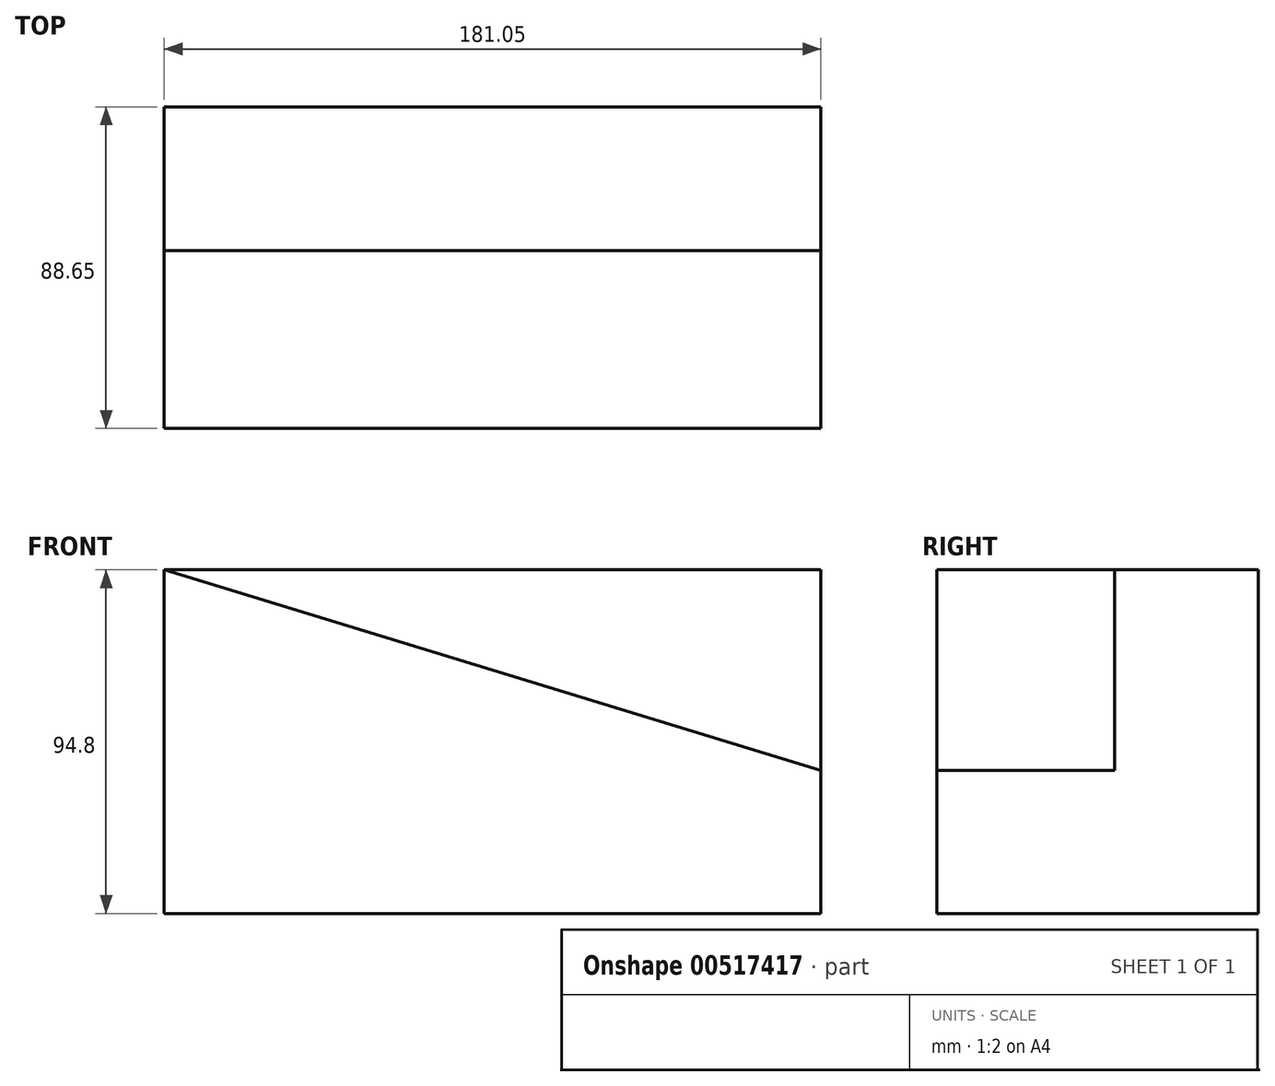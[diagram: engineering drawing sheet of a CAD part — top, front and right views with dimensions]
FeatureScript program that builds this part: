
annotation { "Feature Type Name" : "Feature", "Feature Type Description" : "" }
export const myFeature = defineFeature(function(context is Context, id is Id, definition is map)
    precondition{}
    {
        {
            var Q0;
            Q0=qCreatedBy(makeId("Front.planeOp"),FACE);
            var sketch = newSketch(context, id + "F0", { "sketchPlane" : qUnion([Q0])});
            skLineSegment(sketch, "E0.bottom", {"start": v(-72.85, 19.13) * mm, "end": v(108.2, 19.13) * mm});
            skLineSegment(sketch, "E0.top", {"start": v(-72.85, -75.67) * mm, "end": v(108.2, -75.67) * mm});
            skLineSegment(sketch, "E0.left", {"start": v(-72.85, 19.13) * mm, "end": v(-72.85, -75.67) * mm});
            skLineSegment(sketch, "E0.right", {"start": v(108.2, 19.13) * mm, "end": v(108.2, -75.67) * mm});
            skSolve(sketch);
        }
        {
            var Q0;
            Q0=makeQuery(id+"F0.imprint","IMPRINT",FACE,{"disambiguationData":[TD([[makeQuery(id+"F0.imprint","IMPRINT",EDGE,{"derivedFrom":sQuery(id+"F0.wireOp",EDGE,"E0.bottom")}),-1.0]])]});
            extrude(context, id + "F1", {"entities" : qUnion([Q0]), "depth" : 88.65 * mm, "offsetDistance" : 25.4 * mm});
        }
        {
            var Q0;
            Q0=makeQuery(id+"F1.opExtrude","CAP_FACE",FACE,{"disambiguationData":[OSD([sQuery(id+"F0.wireOp",EDGE,"E0.bottom"),sQuery(id+"F0.wireOp",EDGE,"E0.top"),sQuery(id+"F0.wireOp",EDGE,"E0.left"),sQuery(id+"F0.wireOp",EDGE,"E0.right")])],"isStart":false});
            var sketch = newSketch(context, id + "F2", { "sketchPlane" : qUnion([Q0])});
            skLineSegment(sketch, "E1", {"start": v(-72.85, 19.13) * mm, "end": v(108.2, -36.28) * mm});
            skSolve(sketch);
        }
        {
            var Q0;
            {var subQ0=sQuery(id+"F2.wireOp",EDGE,"E1");Q0=makeQuery(id+"F2.imprint","IMPRINT",FACE,{"disambiguationData":[TD([[makeQuery(id+"F2.imprint","IMPRINT",EDGE,{"derivedFrom":subQ0}),1.0]])]});}
            extrude(context, id + "F3", {"entities" : qUnion([Q0]), "operationType" : NewBodyOperationType.REMOVE, "oppositeDirection" : true, "depth" : 49.02 * mm, "offsetDistance" : 25.4 * mm});
        }
    });
